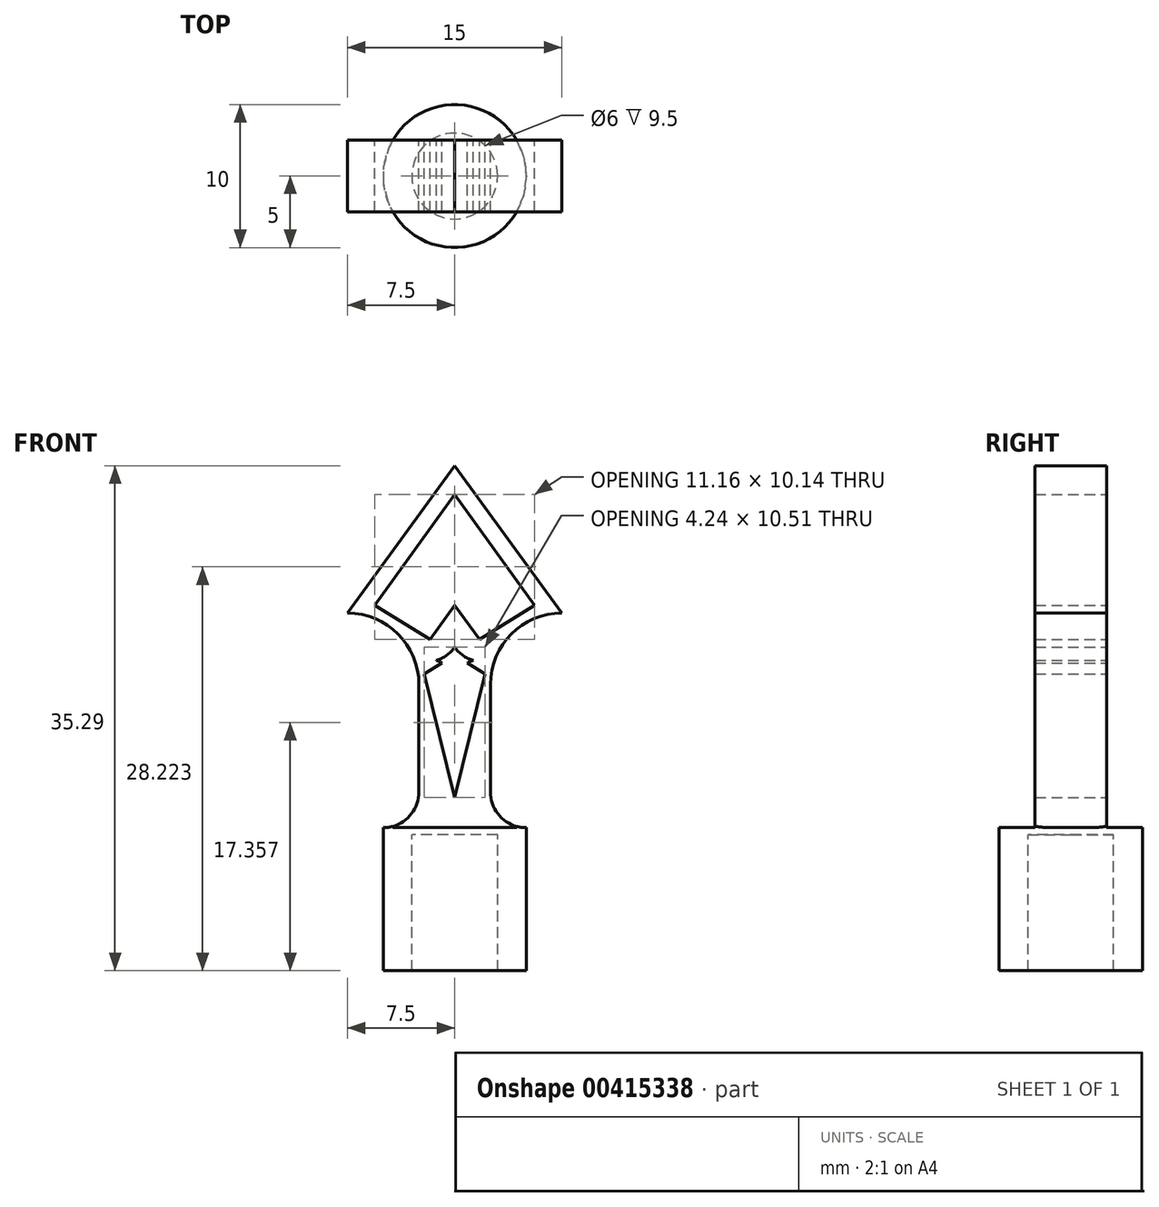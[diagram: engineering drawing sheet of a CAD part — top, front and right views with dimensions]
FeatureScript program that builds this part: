
annotation { "Feature Type Name" : "Feature", "Feature Type Description" : "" }
export const myFeature = defineFeature(function(context is Context, id is Id, definition is map)
    precondition{}
    {
        {
            var Q0;
            Q0=qCreatedBy(makeId("Top.planeOp"),FACE);
            var sketch = newSketch(context, id + "F0", { "sketchPlane" : qUnion([Q0])});
            skCircle(sketch, "E0", {"center": v(0, 0) * mm, "radius": 3 * mm});
            skCircle(sketch, "E1", {"center": v(0, 0) * mm, "radius": 5 * mm});
            skSolve(sketch);
        }
        {
            var Q0;
            Q0=makeQuery(id+"F0.imprint","IMPRINT",FACE,{"disambiguationData":[TD([[makeQuery(id+"F0.imprint","IMPRINT",EDGE,{"derivedFrom":sQuery(id+"F0.wireOp",EDGE,"E0")}),-1.0]])]});
            extrude(context, id + "F1", {"entities" : qUnion([Q0]), "oppositeDirection" : true, "depth" : 10 * mm});
        }
        {
            var Q0;
            Q0=qCreatedBy(makeId("Front.planeOp"),FACE);
            var sketch = newSketch(context, id + "F2", { "sketchPlane" : qUnion([Q0])});
            skLineSegment(sketch, "E2", {"start": v(0, 0) * mm, "end": v(0, 15) * mm});
            skLineSegment(sketch, "E3", {"start": v(0, 15) * mm, "end": v(-2.5, 15) * mm});
            skLineSegment(sketch, "E4", {"start": v(-2.5, 15) * mm, "end": v(-2.5, 0) * mm});
            skLineSegment(sketch, "E5", {"start": v(-2.5, 0) * mm, "end": v(2.5, 0) * mm});
            skLineSegment(sketch, "E6", {"start": v(2.5, 0) * mm, "end": v(2.5, 15) * mm});
            skLineSegment(sketch, "E7", {"start": v(2.5, 15) * mm, "end": v(0, 15) * mm});
            skLineSegment(sketch, "E8", {"start": v(-2.5, 15) * mm, "end": v(-7.5, 15) * mm});
            skLineSegment(sketch, "E9", {"start": v(-7.5, 15) * mm, "end": v(0, 25.3) * mm});
            skLineSegment(sketch, "E10", {"start": v(0, 25.3) * mm, "end": v(7.5, 15) * mm});
            skLineSegment(sketch, "E11", {"start": v(7.5, 15) * mm, "end": v(2.5, 15) * mm});
            skLineSegment(sketch, "E12", {"start": v(-2.5, 15) * mm, "end": v(-2.5, 10) * mm});
            skLineSegment(sketch, "E13", {"start": v(2.5, 15) * mm, "end": v(2.5, 10) * mm});
            skArc(sketch, "E14", {"start": v(-2.5, 10) * mm, "mid": v(-3.96, 13.54) * mm, "end": v(-7.5, 15) * mm});
            skArc(sketch, "E15", {"start": v(7.5, 15) * mm, "mid": v(3.96, 13.54) * mm, "end": v(2.5, 10) * mm});
            skLineSegment(sketch, "E16", {"start": v(-2.5, 0) * mm, "end": v(-5, 0) * mm});
            skLineSegment(sketch, "E17", {"start": v(2.5, 0) * mm, "end": v(5, 0) * mm});
            skLineSegment(sketch, "E18", {"start": v(-2.5, 0) * mm, "end": v(-2.5, 2.5) * mm});
            skLineSegment(sketch, "E19", {"start": v(2.5, 0) * mm, "end": v(2.5, 2.5) * mm});
            skArc(sketch, "E20", {"start": v(-5, 0) * mm, "mid": v(-3.23, 0.73) * mm, "end": v(-2.5, 2.5) * mm});
            skArc(sketch, "E21", {"start": v(2.5, 2.5) * mm, "mid": v(3.23, 0.73) * mm, "end": v(5, 0) * mm});
            skSolve(sketch);
        }
        {
            var Q0;
            Q0 = qSketchRegion(id + "F2", true);
            extrude(context, id + "F3", {"entities" : qUnion([Q0]), "operationType" : NewBodyOperationType.ADD, "endBound" : BoundingType.SYMMETRIC, "depth" : 5 * mm});
        }
        {
            var Q0;
            Q0=makeQuery(id+"F3.opExtrude","CAP_FACE",FACE,{"disambiguationData":[OSD([sQuery(id+"F2.wireOp",EDGE,"E4"),sQuery(id+"F2.wireOp",EDGE,"E5"),sQuery(id+"F2.wireOp",EDGE,"E6"),sQuery(id+"F2.wireOp",EDGE,"E9"),sQuery(id+"F2.wireOp",EDGE,"E10"),sQuery(id+"F2.wireOp",EDGE,"E14"),sQuery(id+"F2.wireOp",EDGE,"E15"),sQuery(id+"F2.wireOp",EDGE,"E16"),sQuery(id+"F2.wireOp",EDGE,"E17"),sQuery(id+"F2.wireOp",EDGE,"E20"),sQuery(id+"F2.wireOp",EDGE,"E21")])],"isStart":true});
            var sketch = newSketch(context, id + "F4", { "sketchPlane" : qUnion([Q0])});
            skLineSegment(sketch, "E22", {"start": v(0, 25.3) * mm, "end": v(0, 23.3) * mm});
            skLineSegment(sketch, "E23", {"start": v(-7.5, 15) * mm, "end": v(-5.58, 15.55) * mm});
            skLineSegment(sketch, "E24", {"start": v(7.5, 15) * mm, "end": v(5.58, 15.55) * mm});
            skLineSegment(sketch, "E25", {"start": v(-5.58, 15.55) * mm, "end": v(5.58, 15.55) * mm});
            skLineSegment(sketch, "E26", {"start": v(-5.58, 15.55) * mm, "end": v(0, 23.3) * mm});
            skLineSegment(sketch, "E27", {"start": v(5.58, 15.55) * mm, "end": v(0, 23.3) * mm});
            skLineSegment(sketch, "E28", {"start": v(-7.5, 15) * mm, "end": v(7.5, 15) * mm});
            skArc(sketch, "E29", {"start": v(5.58, 15.55) * mm, "mid": v(0, 18.4) * mm, "end": v(-5.58, 15.55) * mm});
            skLineSegment(sketch, "E30", {"start": v(0, 23.3) * mm, "end": v(0, 18.4) * mm});
            skLineSegment(sketch, "E31", {"start": v(-5.58, 15.55) * mm, "end": v(0, 7.81) * mm});
            skPoint(sketch, "E31.endSnap0", {"position": v(0, 15) * mm});
            skLineSegment(sketch, "E32", {"start": v(0, 7.81) * mm, "end": v(5.58, 15.55) * mm});
            skLineSegment(sketch, "E33", {"start": v(0, 15.55) * mm, "end": v(-2.79, 11.68) * mm});
            skLineSegment(sketch, "E34", {"start": v(0, 15.55) * mm, "end": v(2.79, 11.68) * mm});
            skArc(sketch, "E35", {"start": v(-2.79, 11.68) * mm, "mid": v(0, 12.61) * mm, "end": v(0, 15.55) * mm});
            skArc(sketch, "E36", {"start": v(2.79, 11.68) * mm, "mid": v(0, 10.75) * mm, "end": v(0, 7.81) * mm});
            skArc(sketch, "E37", {"start": v(0, 15.55) * mm, "mid": v(0, 12.61) * mm, "end": v(2.79, 11.68) * mm});
            skArc(sketch, "E38", {"start": v(0, 7.81) * mm, "mid": v(0, 10.75) * mm, "end": v(-2.79, 11.68) * mm});
            skLineSegment(sketch, "E39", {"start": v(-5.58, 15.55) * mm, "end": v(2.12, 10.75) * mm});
            skPoint(sketch, "E39.endSnap0", {"position": v(0, 10.75) * mm});
            skLineSegment(sketch, "E40", {"start": v(2.12, 10.75) * mm, "end": v(-2.12, 10.75) * mm});
            skLineSegment(sketch, "E41", {"start": v(-2.12, 10.75) * mm, "end": v(5.58, 15.55) * mm});
            skLineSegment(sketch, "E42", {"start": v(2.12, 10.75) * mm, "end": v(0, 2.1) * mm});
            skLineSegment(sketch, "E43", {"start": v(0, 2.1) * mm, "end": v(-2.12, 10.75) * mm});
            skSolve(sketch);
        }
        {
            var Q0;
            {var subQ0=sQuery(id+"F4.wireOp",EDGE,"E26");Q0=makeQuery(id+"F4.imprint","IMPRINT",FACE,{"disambiguationData":[TD([[makeQuery(id+"F4.imprint","IMPRINT",EDGE,{"derivedFrom":subQ0}),-1.0]])]});}
            var Q1;
            {var subQ0=sQuery(id+"F4.wireOp",EDGE,"E27");Q1=makeQuery(id+"F4.imprint","IMPRINT",FACE,{"disambiguationData":[TD([[makeQuery(id+"F4.imprint","IMPRINT",EDGE,{"derivedFrom":subQ0}),1.0]])]});}
            var Q2;
            {var subQ0=sQuery(id+"F4.wireOp",EDGE,"E29");var subQ5=makeQuery(id+"F4.imprint","INTERSECT",VERTEX,{"derivedFrom":[subQ0,sQuery(id+"F4.wireOp",EDGE,"E30")]});Q2=makeQuery(id+"F4.imprint","IMPRINT",FACE,{"disambiguationData":[TD([[makeQuery(id+"F4.imprint","IMPRINT",EDGE,{"disambiguationData":[TD([[subQ5,1.0]])],"derivedFrom":subQ0}),1.0]])]});}
            var Q3;
            {var subQ0=sQuery(id+"F4.wireOp",EDGE,"E39");var subQ5=sQuery(id+"F4.wireOp",EDGE,"E28");var subQ6=makeQuery(id+"F4.imprint","INTERSECT",VERTEX,{"derivedFrom":[subQ5,subQ0]});Q3=makeQuery(id+"F4.imprint","IMPRINT",FACE,{"disambiguationData":[TD([[makeQuery(id+"F4.imprint","IMPRINT",EDGE,{"disambiguationData":[TD([[subQ6,-1.0]])],"derivedFrom":subQ5}),1.0]])]});}
            var Q4;
            {var subQ3=sQuery(id+"F4.wireOp",EDGE,"E34");var subQ5=sQuery(id+"F4.wireOp",EDGE,"E28");var subQ6=makeQuery(id+"F4.imprint","INTERSECT",VERTEX,{"derivedFrom":[subQ5,subQ3]});Q4=makeQuery(id+"F4.imprint","IMPRINT",FACE,{"disambiguationData":[TD([[makeQuery(id+"F4.imprint","IMPRINT",EDGE,{"disambiguationData":[TD([[subQ6,-1.0]])],"derivedFrom":subQ5}),1.0]])]});}
            var Q5;
            {var subQ0=sQuery(id+"F4.wireOp",EDGE,"E39");var subQ1=sQuery(id+"F4.wireOp",EDGE,"E28");var subQ2=makeQuery(id+"F4.imprint","INTERSECT",VERTEX,{"derivedFrom":[subQ1,subQ0]});Q5=makeQuery(id+"F4.imprint","IMPRINT",FACE,{"disambiguationData":[TD([[makeQuery(id+"F4.imprint","IMPRINT",EDGE,{"disambiguationData":[TD([[subQ2,-1.0]])],"derivedFrom":subQ1}),-1.0]])]});}
            var Q6;
            {var subQ0=sQuery(id+"F4.wireOp",EDGE,"E34");var subQ1=sQuery(id+"F4.wireOp",EDGE,"E28");var subQ2=makeQuery(id+"F4.imprint","INTERSECT",VERTEX,{"derivedFrom":[subQ1,subQ0]});Q6=makeQuery(id+"F4.imprint","IMPRINT",FACE,{"disambiguationData":[TD([[makeQuery(id+"F4.imprint","IMPRINT",EDGE,{"disambiguationData":[TD([[subQ2,-1.0]])],"derivedFrom":subQ1}),-1.0]])]});}
            var Q7;
            {var subQ0=sQuery(id+"F4.wireOp",EDGE,"E41");var subQ1=sQuery(id+"F4.wireOp",EDGE,"E38");var subQ2=makeQuery(id+"F4.imprint","INTERSECT",VERTEX,{"derivedFrom":[subQ1,subQ0]});Q7=makeQuery(id+"F4.imprint","IMPRINT",FACE,{"disambiguationData":[TD([[makeQuery(id+"F4.imprint","IMPRINT",EDGE,{"disambiguationData":[TD([[subQ2,1.0]])],"derivedFrom":subQ1}),1.0]])]});}
            var Q8;
            {var subQ2=sQuery(id+"F4.wireOp",EDGE,"E31");var subQ4=sQuery(id+"F4.wireOp",EDGE,"E40");var subQ5=makeQuery(id+"F4.imprint","INTERSECT",VERTEX,{"derivedFrom":[subQ2,subQ4,sQuery(id+"F4.wireOp",EDGE,"E41")]});Q8=makeQuery(id+"F4.imprint","IMPRINT",FACE,{"disambiguationData":[TD([[makeQuery(id+"F4.imprint","IMPRINT",EDGE,{"disambiguationData":[TD([[subQ5,1.0]])],"derivedFrom":subQ4}),1.0]])]});}
            var Q9;
            {var subQ0=sQuery(id+"F4.wireOp",EDGE,"E38");var subQ1=sQuery(id+"F4.wireOp",EDGE,"E36");var subQ3=makeQuery(id+"F4.imprint","INTERSECT",VERTEX,{"derivedFrom":[subQ1,subQ0,sQuery(id+"F4.wireOp",EDGE,"E40")]});Q9=makeQuery(id+"F4.imprint","IMPRINT",FACE,{"disambiguationData":[TD([[makeQuery(id+"F4.imprint","IMPRINT",EDGE,{"disambiguationData":[TD([[subQ3,-1.0]])],"derivedFrom":subQ1}),1.0]])]});}
            var Q10;
            {var subQ2=sQuery(id+"F4.wireOp",EDGE,"E32");var subQ4=sQuery(id+"F4.wireOp",EDGE,"E40");var subQ5=makeQuery(id+"F4.imprint","INTERSECT",VERTEX,{"derivedFrom":[subQ2,sQuery(id+"F4.wireOp",EDGE,"E39"),subQ4]});Q10=makeQuery(id+"F4.imprint","IMPRINT",FACE,{"disambiguationData":[TD([[makeQuery(id+"F4.imprint","IMPRINT",EDGE,{"disambiguationData":[TD([[subQ5,-1.0]])],"derivedFrom":subQ4}),1.0]])]});}
            var Q11;
            {var subQ0=sQuery(id+"F4.wireOp",EDGE,"E39");var subQ1=sQuery(id+"F4.wireOp",EDGE,"E36");var subQ2=makeQuery(id+"F4.imprint","INTERSECT",VERTEX,{"derivedFrom":[subQ1,subQ0]});Q11=makeQuery(id+"F4.imprint","IMPRINT",FACE,{"disambiguationData":[TD([[makeQuery(id+"F4.imprint","IMPRINT",EDGE,{"disambiguationData":[TD([[subQ2,-1.0]])],"derivedFrom":subQ1}),1.0]])]});}
            var Q12;
            {var subQ1=sQuery(id+"F4.wireOp",EDGE,"E35");var subQ3=sQuery(id+"F4.wireOp",EDGE,"E39");var subQ4=makeQuery(id+"F4.imprint","INTERSECT",VERTEX,{"derivedFrom":[subQ1,subQ3]});Q12=makeQuery(id+"F4.imprint","IMPRINT",FACE,{"disambiguationData":[TD([[makeQuery(id+"F4.imprint","IMPRINT",EDGE,{"disambiguationData":[TD([[subQ4,-1.0]])],"derivedFrom":subQ3}),-1.0]])]});}
            var Q13;
            {var subQ1=sQuery(id+"F4.wireOp",EDGE,"E36");var subQ3=sQuery(id+"F4.wireOp",EDGE,"E39");var subQ4=makeQuery(id+"F4.imprint","INTERSECT",VERTEX,{"derivedFrom":[subQ1,subQ3]});Q13=makeQuery(id+"F4.imprint","IMPRINT",FACE,{"disambiguationData":[TD([[makeQuery(id+"F4.imprint","IMPRINT",EDGE,{"disambiguationData":[TD([[subQ4,1.0]])],"derivedFrom":subQ3}),1.0]])]});}
            var Q14;
            {var subQ0=sQuery(id+"F4.wireOp",EDGE,"E39");var subQ1=sQuery(id+"F4.wireOp",EDGE,"E36");var subQ2=makeQuery(id+"F4.imprint","INTERSECT",VERTEX,{"derivedFrom":[subQ1,subQ0]});Q14=makeQuery(id+"F4.imprint","IMPRINT",FACE,{"disambiguationData":[TD([[makeQuery(id+"F4.imprint","IMPRINT",EDGE,{"disambiguationData":[TD([[subQ2,1.0]])],"derivedFrom":subQ0}),-1.0]])]});}
            var Q15;
            {var subQ0=sQuery(id+"F4.wireOp",EDGE,"E39");var subQ1=sQuery(id+"F4.wireOp",EDGE,"E35");var subQ2=makeQuery(id+"F4.imprint","INTERSECT",VERTEX,{"derivedFrom":[subQ1,subQ0]});Q15=makeQuery(id+"F4.imprint","IMPRINT",FACE,{"disambiguationData":[TD([[makeQuery(id+"F4.imprint","IMPRINT",EDGE,{"disambiguationData":[TD([[subQ2,-1.0]])],"derivedFrom":subQ1}),-1.0]])]});}
            var Q16;
            {var subQ5=sQuery(id+"F4.wireOp",EDGE,"E42");Q16=makeQuery(id+"F4.imprint","IMPRINT",FACE,{"disambiguationData":[TD([[makeQuery(id+"F4.imprint","IMPRINT",EDGE,{"derivedFrom":subQ5}),-1.0]])]});}
            extrude(context, id + "F5", {"entities" : qUnion([Q0, Q1, Q2, Q3, Q4, Q5, Q6, Q7, Q8, Q9, Q10, Q11, Q12, Q13, Q14, Q15, Q16]), "operationType" : NewBodyOperationType.REMOVE, "oppositeDirection" : true, "depth" : 25 * mm});
        }
        {
            var Q0;
            Q0=makeQuery(id+"F1.opExtrude","CAP_FACE",FACE,{"disambiguationData":[OSD([sQuery(id+"F0.wireOp",EDGE,"E0"),sQuery(id+"F0.wireOp",EDGE,"E1")])],"isStart":false});
            var sketch = newSketch(context, id + "F6", { "sketchPlane" : qUnion([Q0])});
            skCircle(sketch, "E44", {"center": v(0, 0) * mm, "radius": 5 * mm});
            skCircle(sketch, "E45", {"center": v(0, 0) * mm, "radius": 7.5 * mm});
            skSolve(sketch);
        }
        {
            var Q0;
            Q0=makeQuery(id+"F6.imprint","IMPRINT",FACE,{"disambiguationData":[TD([[makeQuery(id+"F6.imprint","IMPRINT",EDGE,{"derivedFrom":sQuery(id+"F6.wireOp",EDGE,"E44")}),-1.0]])]});
            extrude(context, id + "F7", {"entities" : qUnion([Q0]), "operationType" : NewBodyOperationType.REMOVE, "oppositeDirection" : true, "depth" : 15 * mm});
        }
        {
            var Q0;
            {var subQ0=sQuery(id+"F0.wireOp",EDGE,"E0");var subQ1=sQuery(id+"F2.wireOp",EDGE,"E17");var subQ2=sQuery(id+"F2.wireOp",EDGE,"E16");var subQ3=sQuery(id+"F2.wireOp",EDGE,"E5");var subQ4=sQuery(id+"F0.wireOp",EDGE,"E1");Q0=makeQuery(id+"F3.boolean.opBoolean","SPLIT",FACE,{"disambiguationData":[TD([makeQuery(id+"F3.opExtrude","CAP_FACE",FACE,{"disambiguationData":[OSD([sQuery(id+"F2.wireOp",EDGE,"E4"),subQ3,sQuery(id+"F2.wireOp",EDGE,"E6"),sQuery(id+"F2.wireOp",EDGE,"E9"),sQuery(id+"F2.wireOp",EDGE,"E10"),sQuery(id+"F2.wireOp",EDGE,"E14"),sQuery(id+"F2.wireOp",EDGE,"E15"),subQ2,subQ1,sQuery(id+"F2.wireOp",EDGE,"E20"),sQuery(id+"F2.wireOp",EDGE,"E21")])],"isStart":false})])],"derivedFrom":makeQuery(id+"F1.opExtrude","CAP_FACE",FACE,{"disambiguationData":[OSD([subQ0,subQ4])],"isStart":true})});}
            var sketch = newSketch(context, id + "F8", { "sketchPlane" : qUnion([Q0])});
            skCircle(sketch, "E46", {"center": v(0, 0) * mm, "radius": 4 * mm});
            skSolve(sketch);
        }
        {
            var Q0;
            {var subQ1=sQuery(id+"F0.wireOp",EDGE,"E0");var subQ2=makeQuery(id+"F1.opExtrude","CAP_FACE",FACE,{"disambiguationData":[OSD([subQ1,sQuery(id+"F0.wireOp",EDGE,"E1")])],"isStart":true});var subQ3=sQuery(id+"F2.wireOp",EDGE,"E17");var subQ4=sQuery(id+"F2.wireOp",EDGE,"E16");var subQ5=sQuery(id+"F2.wireOp",EDGE,"E5");var subQ6=makeQuery(id+"F3.opExtrude","CAP_FACE",FACE,{"disambiguationData":[OSD([sQuery(id+"F2.wireOp",EDGE,"E4"),subQ5,sQuery(id+"F2.wireOp",EDGE,"E6"),sQuery(id+"F2.wireOp",EDGE,"E9"),sQuery(id+"F2.wireOp",EDGE,"E10"),sQuery(id+"F2.wireOp",EDGE,"E14"),sQuery(id+"F2.wireOp",EDGE,"E15"),subQ4,subQ3,sQuery(id+"F2.wireOp",EDGE,"E20"),sQuery(id+"F2.wireOp",EDGE,"E21")])],"isStart":false});var subQ12=makeQuery(id+"F1.opExtrude","SWEPT_FACE",FACE,{"disambiguationData":[OSD([subQ1])]});var subQ13=makeQuery(id+"F3.boolean.opBoolean","SPLIT",EDGE,{"disambiguationData":[topologyDisambiguationEdgeConnected([subQ12,subQ2]),TD([subQ6])],"derivedFrom":makeQuery(id+"F1.opExtrude","CAP_EDGE",EDGE,{"disambiguationData":[OSD([subQ1])],"isStart":true})});Q0=makeQuery(id+"F8.imprint","IMPRINT",FACE,{"disambiguationData":[TD([[makeQuery(id+"F8.imprint","IMPRINT",EDGE,{"derivedFrom":subQ13}),1.0]])]});}
            extrude(context, id + "F9", {"entities" : qUnion([Q0]), "operationType" : NewBodyOperationType.ADD, "oppositeDirection" : true, "depth" : 0.5 * mm});
        }
    });
